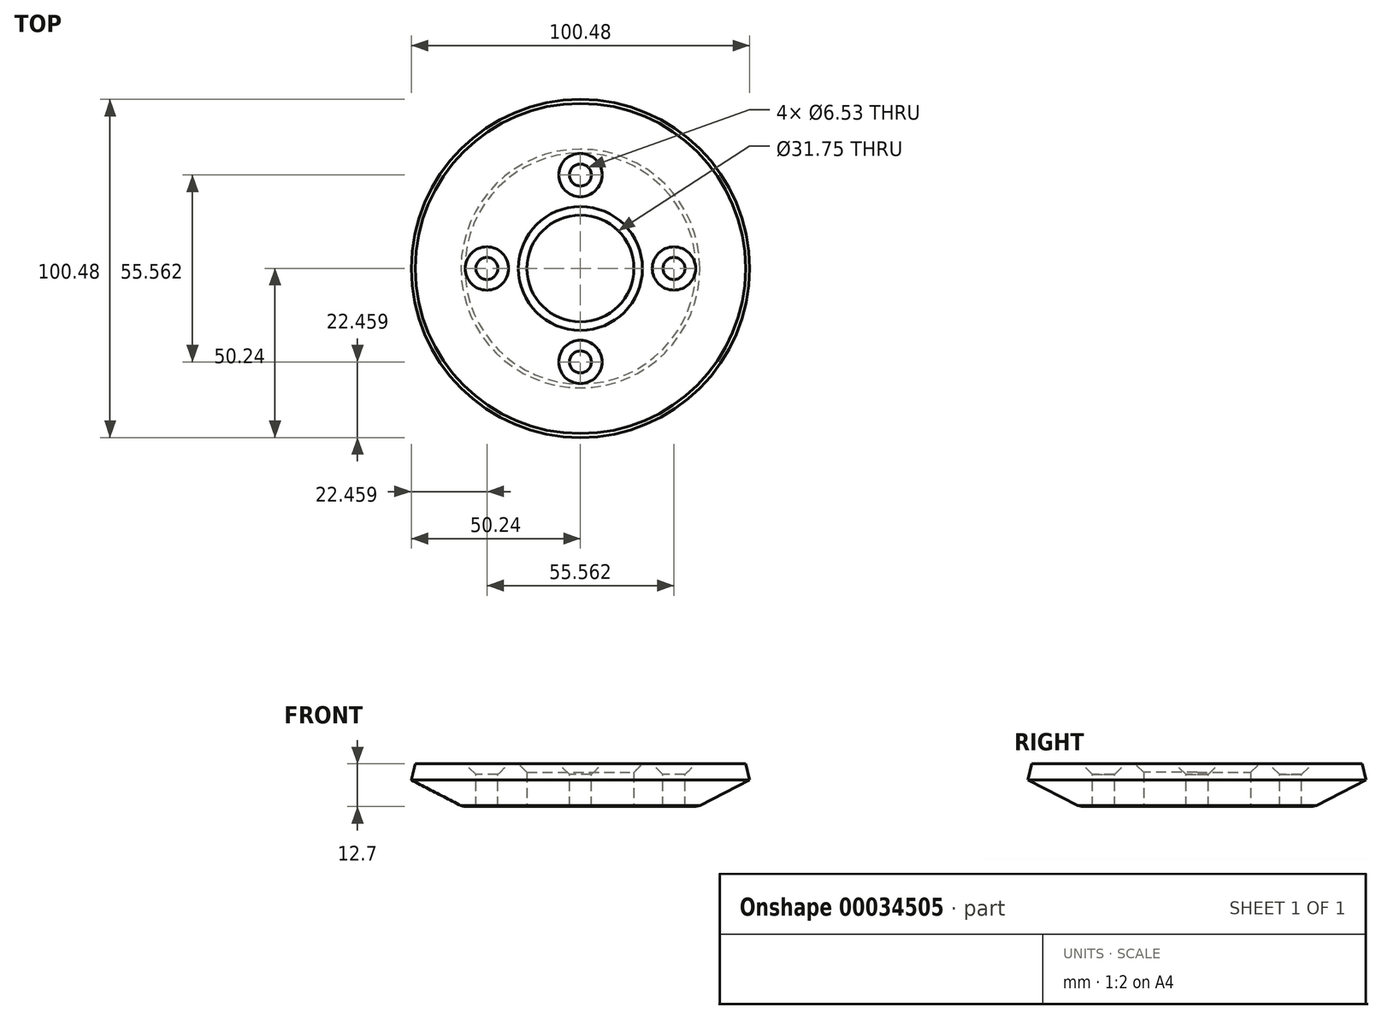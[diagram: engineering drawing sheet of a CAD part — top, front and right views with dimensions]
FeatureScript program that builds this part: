
annotation { "Feature Type Name" : "Feature", "Feature Type Description" : "" }
export const myFeature = defineFeature(function(context is Context, id is Id, definition is map)
    precondition{}
    {
        {
            var Q0;
            Q0=qCreatedBy(makeId("Front.planeOp"),FACE);
            var sketch = newSketch(context, id + "F0", { "sketchPlane" : qUnion([Q0])});
            skLineSegment(sketch, "E0", {"start": v(-34.92, 0) * mm, "end": v(-59.53, 12.7) * mm});
            skLineSegment(sketch, "E1", {"start": v(-59.53, 12.7) * mm, "end": v(-15.88, 12.7) * mm});
            skLineSegment(sketch, "E2", {"start": v(-15.88, 12.7) * mm, "end": v(-15.88, 0) * mm});
            skLineSegment(sketch, "E3", {"start": v(-15.88, 0) * mm, "end": v(-34.92, 0) * mm});
            skLineSegment(sketch, "E4", {"start": v(0, 0) * mm, "end": v(0, 47.87) * mm, "construction": true});
            skSolve(sketch);
        }
        {
            var Q0;
            Q0=makeQuery(id+"F0.imprint","IMPRINT",FACE,{"disambiguationData":[TD([[makeQuery(id+"F0.imprint","IMPRINT",EDGE,{"derivedFrom":sQuery(id+"F0.wireOp",EDGE,"E0")}),-1.0]])]});
            var Q1;
            Q1=sQuery(id+"F0.wireOp",EDGE,"E1");
            var Q2;
            Q2=sQuery(id+"F0.wireOp",EDGE,"E2");
            var Q3;
            Q3=sQuery(id+"F0.wireOp",EDGE,"E3");
            var Q4;
            Q4=sQuery(id+"F0.wireOp",EDGE,"E0");
            var Q5;
            Q5=sQuery(id+"F0.wireOp",EDGE,"E4");
            revolve(context, id + "F1", {"entities" : qUnion([Q0]), "surfaceEntities" : qUnion([Q1, Q2, Q3, Q4]), "axis" : qUnion([Q5]), "revolveType" : RevolveType.FULL});
        }
        {
            var Q0;
            Q0=makeQuery(id+"F1.opRevolve","SWEPT_FACE",FACE,{"disambiguationData":[OSD([sQuery(id+"F0.wireOp",EDGE,"E1")])]});
            var sketch = newSketch(context, id + "F2", { "sketchPlane" : qUnion([Q0])});
            skPoint(sketch, "E5", {"position": v(27.78, 0) * mm});
            skPoint(sketch, "E6", {"position": v(0, 27.78) * mm});
            skPoint(sketch, "E7", {"position": v(-27.78, 0) * mm});
            skPoint(sketch, "E8", {"position": v(0, -27.78) * mm});
            skSolve(sketch);
        }
        {
            var Q0;
            Q0=sQuery(id+"F2.wireOp",VERTEX,"E6");
            var Q1;
            Q1=sQuery(id+"F2.wireOp",VERTEX,"E5");
            var Q2;
            Q2=sQuery(id+"F2.wireOp",VERTEX,"E8");
            var Q3;
            Q3=sQuery(id+"F2.wireOp",VERTEX,"E7");
            var Q4;
            Q4=makeQuery(id+"F1.opRevolve","SWEPT_BODY",BODY,{"disambiguationData":[OSD([sQuery(id+"F0.wireOp",EDGE,"E0"),sQuery(id+"F0.wireOp",EDGE,"E1"),sQuery(id+"F0.wireOp",EDGE,"E2"),sQuery(id+"F0.wireOp",EDGE,"E3")])]});
            hole(context, id + "F3", {"style" : HoleStyle.C_SINK, "holeDiameter" : 6.53 * mm, "cSinkDiameter" : 12.88 * mm, "endStyle" : HoleEndStyle.THROUGH, "locations" : qUnion([Q0, Q1, Q2, Q3]), "scope" : qUnion([Q4]), "cSinkAngle" : 90 * degree});
        }
        {
            var Q0;
            Q0=makeQuery(id+"F1.opRevolve","SWEPT_EDGE",EDGE,{"disambiguationData":[OSD([sQuery(id+"F0.wireOp",EDGE,"E0"),sQuery(id+"F0.wireOp",EDGE,"E1")])]});
            var Q1;
            Q1=makeQuery(id+"F3.hole-1.boolean.opBoolean","INTERSECT",EDGE,{"derivedFrom":[makeQuery(id+"F1.opRevolve","SWEPT_FACE",FACE,{"disambiguationData":[OSD([sQuery(id+"F0.wireOp",EDGE,"E1")])]}),makeQuery(id+"F3.hole-1.opRevolve","SWEPT_FACE",FACE,{"disambiguationData":[OSD([sQuery(id+"F3.hole-1.sketch.wireOp",EDGE,"core_line_2")])]})]});
            var Q2;
            Q2=makeQuery(id+"F3.hole-0.boolean.opBoolean","INTERSECT",EDGE,{"derivedFrom":[makeQuery(id+"F1.opRevolve","SWEPT_FACE",FACE,{"disambiguationData":[OSD([sQuery(id+"F0.wireOp",EDGE,"E1")])]}),makeQuery(id+"F3.hole-0.opRevolve","SWEPT_FACE",FACE,{"disambiguationData":[OSD([sQuery(id+"F3.hole-0.sketch.wireOp",EDGE,"core_line_2")])]})]});
            var Q3;
            Q3=makeQuery(id+"F3.hole-3.boolean.opBoolean","INTERSECT",EDGE,{"derivedFrom":[makeQuery(id+"F1.opRevolve","SWEPT_FACE",FACE,{"disambiguationData":[OSD([sQuery(id+"F0.wireOp",EDGE,"E1")])]}),makeQuery(id+"F3.hole-3.opRevolve","SWEPT_FACE",FACE,{"disambiguationData":[OSD([sQuery(id+"F3.hole-3.sketch.wireOp",EDGE,"core_line_2")])]})]});
            var Q4;
            Q4=makeQuery(id+"F1.opRevolve","SWEPT_EDGE",EDGE,{"disambiguationData":[OSD([sQuery(id+"F0.wireOp",EDGE,"E1"),sQuery(id+"F0.wireOp",EDGE,"E2")])]});
            var Q5;
            Q5=makeQuery(id+"F3.hole-2.boolean.opBoolean","INTERSECT",EDGE,{"derivedFrom":[makeQuery(id+"F1.opRevolve","SWEPT_FACE",FACE,{"disambiguationData":[OSD([sQuery(id+"F0.wireOp",EDGE,"E1")])]}),makeQuery(id+"F3.hole-2.opRevolve","SWEPT_FACE",FACE,{"disambiguationData":[OSD([sQuery(id+"F3.hole-2.sketch.wireOp",EDGE,"core_line_2")])]})]});
            var Q6;
            Q6=makeQuery(id+"F1.opRevolve","SWEPT_EDGE",EDGE,{"disambiguationData":[OSD([sQuery(id+"F0.wireOp",EDGE,"E0"),sQuery(id+"F0.wireOp",EDGE,"E3")])]});
            var Q7;
            Q7=makeQuery(id+"F3.hole-1.boolean.opBoolean","COPY",EDGE,{"derivedFrom":makeQuery(id+"F3.hole-1.opRevolve","SWEPT_EDGE",EDGE,{"disambiguationData":[OSD([sQuery(id+"F3.hole-1.sketch.wireOp",EDGE,"csink_start_line_1"),sQuery(id+"F3.hole-1.sketch.wireOp",EDGE,"csink_start_line_2")])]})});
            var Q8;
            Q8=makeQuery(id+"F3.hole-2.boolean.opBoolean","COPY",EDGE,{"derivedFrom":makeQuery(id+"F3.hole-2.opRevolve","SWEPT_EDGE",EDGE,{"disambiguationData":[OSD([sQuery(id+"F3.hole-2.sketch.wireOp",EDGE,"csink_start_line_1"),sQuery(id+"F3.hole-2.sketch.wireOp",EDGE,"csink_start_line_2")])]})});
            var Q9;
            Q9=makeQuery(id+"F3.hole-3.boolean.opBoolean","COPY",EDGE,{"derivedFrom":makeQuery(id+"F3.hole-3.opRevolve","SWEPT_EDGE",EDGE,{"disambiguationData":[OSD([sQuery(id+"F3.hole-3.sketch.wireOp",EDGE,"csink_start_line_1"),sQuery(id+"F3.hole-3.sketch.wireOp",EDGE,"csink_start_line_2")])]})});
            var Q10;
            Q10=makeQuery(id+"F3.hole-0.boolean.opBoolean","COPY",EDGE,{"derivedFrom":makeQuery(id+"F3.hole-0.opRevolve","SWEPT_EDGE",EDGE,{"disambiguationData":[OSD([sQuery(id+"F3.hole-0.sketch.wireOp",EDGE,"csink_start_line_1"),sQuery(id+"F3.hole-0.sketch.wireOp",EDGE,"csink_start_line_2")])]})});
            chamfer(context, id + "F4", {"entities" : qUnion([Q0, Q1, Q2, Q3, Q4, Q5, Q6, Q7, Q8, Q9, Q10]), "width" : 2.54 * mm, "tangentPropagation" : true});
        }
    });
